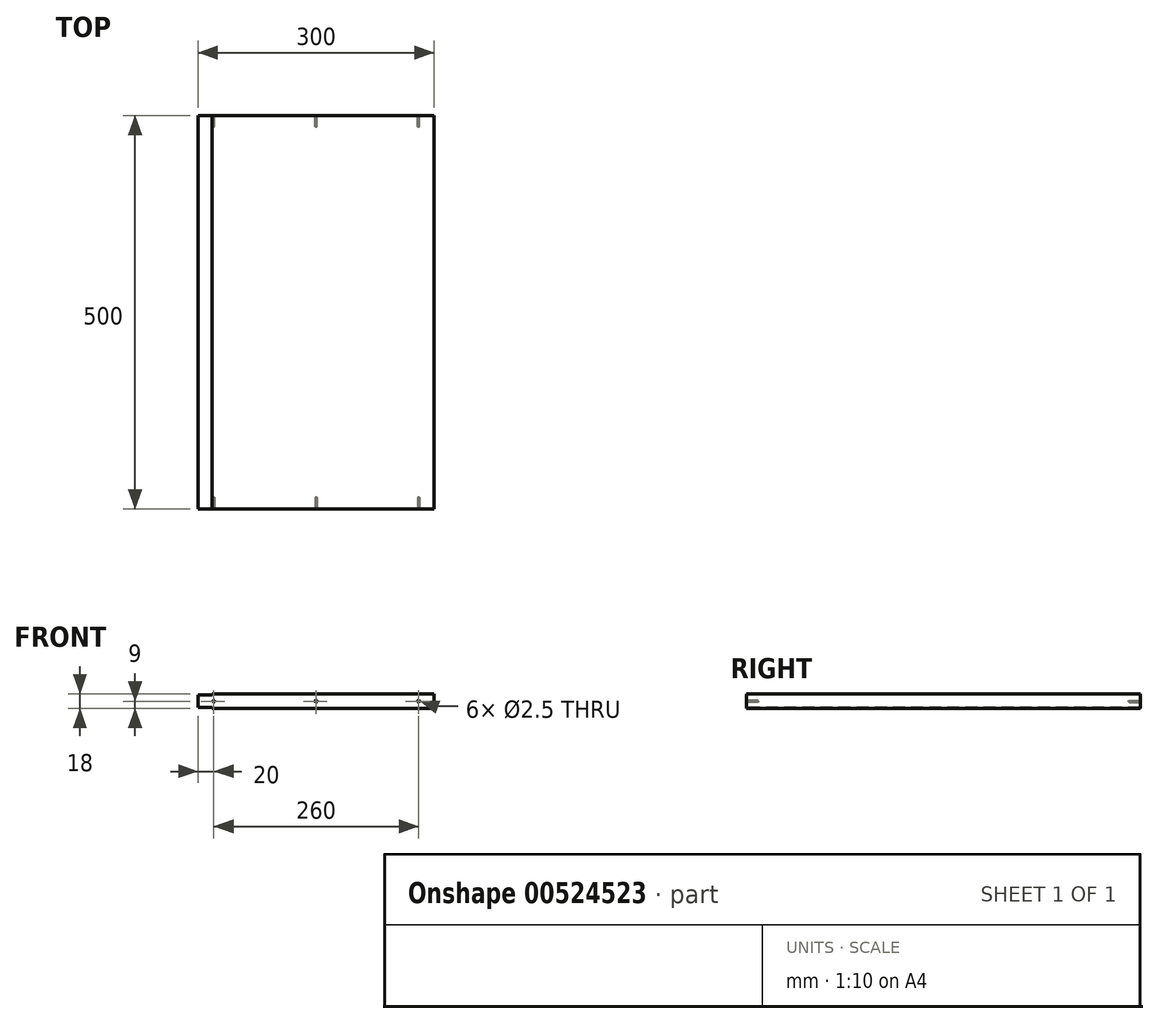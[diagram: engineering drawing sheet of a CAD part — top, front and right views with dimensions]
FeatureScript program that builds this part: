
annotation { "Feature Type Name" : "Feature", "Feature Type Description" : "" }
export const myFeature = defineFeature(function(context is Context, id is Id, definition is map)
    precondition{}
    {
        {
            var Q0;
            Q0=qCreatedBy(makeId("Top.planeOp"),FACE);
            var sketch = newSketch(context, id + "F0", { "sketchPlane" : qUnion([Q0])});
            skLineSegment(sketch, "E0.bottom", {"start": v(0, 0) * mm, "end": v(300, 0) * mm});
            skLineSegment(sketch, "E0.top", {"start": v(0, -500) * mm, "end": v(300, -500) * mm});
            skLineSegment(sketch, "E0.left", {"start": v(0, 0) * mm, "end": v(0, -500) * mm});
            skLineSegment(sketch, "E0.right", {"start": v(300, 0) * mm, "end": v(300, -500) * mm});
            skSolve(sketch);
        }
        {
            var Q0;
            Q0=qSketchRegion(id+"F0",true);
            extrude(context, id + "F1", {"entities" : qUnion([Q0]), "depth" : 18 * mm, "offsetDistance" : 25 * mm});
        }
        {
            var Q0;
            Q0=makeQuery(id+"F1.opExtrude","SWEPT_FACE",FACE,{"disambiguationData":[OSD([sQuery(id+"F0.wireOp",EDGE,"E0.top")])]});
            var sketch = newSketch(context, id + "F2", { "sketchPlane" : qUnion([Q0])});
            skPoint(sketch, "E1", {"position": v(20, 9) * mm});
            skPoint(sketch, "E2", {"position": v(150, 9) * mm});
            skPoint(sketch, "E3", {"position": v(280, 9) * mm});
            skSolve(sketch);
        }
        {
            var Q0;
            Q0=sQuery(id+"F2.wireOp",VERTEX,"E1");
            var Q1;
            Q1=sQuery(id+"F2.wireOp",VERTEX,"E2");
            var Q2;
            Q2=sQuery(id+"F2.wireOp",VERTEX,"E3");
            var Q3;
            Q3=makeQuery(id+"F1.opExtrude","SWEPT_BODY",BODY,{"disambiguationData":[OSD([sQuery(id+"F0.wireOp",EDGE,"E0.bottom"),sQuery(id+"F0.wireOp",EDGE,"E0.top"),sQuery(id+"F0.wireOp",EDGE,"E0.left"),sQuery(id+"F0.wireOp",EDGE,"E0.right")])]});
            hole(context, id + "F3", {"style" : HoleStyle.SIMPLE, "endStyle" : HoleEndStyle.BLIND, "standardTappedOrClearance" : lookupTablePath({ "standard" : "ISO", "engagement" : "75%", "pitch" : "0.5 mm", "size" : "M3", "type" : "Tapped" }), "standardBlindInLast" : lookupTablePath({ "standard" : "ISO", "engagement" : "75%", "pitch" : "0.5 mm", "size" : "M3", "type" : "Tapped" }), "holeDiameter" : 2.5 * mm, "showTappedDepth" : true, "holeDepth" : 14.5 * mm, "isTappedThrough" : true, "tappedDepth" : 13 * mm, "tapClearance" : 3, "locations" : qUnion([Q0, Q1, Q2]), "scope" : qUnion([Q3]), "majorDiameter" : 3 * mm});
        }
        {
            var Q0;
            Q0=makeQuery(id+"F1.opExtrude","SWEPT_FACE",FACE,{"disambiguationData":[OSD([sQuery(id+"F0.wireOp",EDGE,"E0.bottom")])]});
            var sketch = newSketch(context, id + "F4", { "sketchPlane" : qUnion([Q0])});
            skPoint(sketch, "E4", {"position": v(-280, 9) * mm});
            skPoint(sketch, "E5", {"position": v(-150, 9) * mm});
            skPoint(sketch, "E6", {"position": v(-20, 9) * mm});
            skSolve(sketch);
        }
        {
            var Q0;
            Q0=sQuery(id+"F4.wireOp",VERTEX,"E4");
            var Q1;
            Q1=sQuery(id+"F4.wireOp",VERTEX,"E5");
            var Q2;
            Q2=sQuery(id+"F4.wireOp",VERTEX,"E6");
            var Q3;
            Q3=makeQuery(id+"F1.opExtrude","SWEPT_BODY",BODY,{"disambiguationData":[OSD([sQuery(id+"F0.wireOp",EDGE,"E0.bottom"),sQuery(id+"F0.wireOp",EDGE,"E0.top"),sQuery(id+"F0.wireOp",EDGE,"E0.left"),sQuery(id+"F0.wireOp",EDGE,"E0.right")])]});
            hole(context, id + "F5", {"style" : HoleStyle.SIMPLE, "endStyle" : HoleEndStyle.BLIND, "standardTappedOrClearance" : lookupTablePath({ "standard" : "ISO", "engagement" : "75%", "pitch" : "0.5 mm", "size" : "M3", "type" : "Tapped" }), "standardBlindInLast" : lookupTablePath({ "standard" : "ISO", "engagement" : "75%", "pitch" : "0.5 mm", "size" : "M3", "type" : "Tapped" }), "holeDiameter" : 2.5 * mm, "showTappedDepth" : true, "holeDepth" : 14 * mm, "isTappedThrough" : true, "tappedDepth" : 12.5 * mm, "tapClearance" : 3, "locations" : qUnion([Q0, Q1, Q2]), "scope" : qUnion([Q3]), "majorDiameter" : 3 * mm});
        }
        {
            var Q0;
            Q0=makeQuery(id+"F1.opExtrude","SWEPT_FACE",FACE,{"disambiguationData":[OSD([sQuery(id+"F0.wireOp",EDGE,"E0.top")])]});
            var sketch = newSketch(context, id + "F6", { "sketchPlane" : qUnion([Q0])});
            skLineSegment(sketch, "E7.bottom", {"start": v(0, 18) * mm, "end": v(18, 18) * mm});
            skLineSegment(sketch, "E7.top", {"start": v(0, 17) * mm, "end": v(18, 17) * mm});
            skLineSegment(sketch, "E7.left", {"start": v(0, 18) * mm, "end": v(0, 17) * mm});
            skLineSegment(sketch, "E7.right", {"start": v(18, 18) * mm, "end": v(18, 17) * mm});
            skLineSegment(sketch, "E8.bottom", {"start": v(0, 0) * mm, "end": v(18, 0) * mm});
            skLineSegment(sketch, "E8.top", {"start": v(0, 1) * mm, "end": v(18, 1) * mm});
            skLineSegment(sketch, "E8.left", {"start": v(0, 0) * mm, "end": v(0, 1) * mm});
            skLineSegment(sketch, "E8.right", {"start": v(18, 0) * mm, "end": v(18, 1) * mm});
            skSolve(sketch);
        }
        {
            var Q0;
            Q0 = qSketchRegion(id + "F6", true);
            extrude(context, id + "F7", {"entities" : qUnion([Q0]), "operationType" : NewBodyOperationType.REMOVE, "endBound" : BoundingType.THROUGH_ALL, "oppositeDirection" : true, "depth" : 25 * mm, "offsetDistance" : 25 * mm});
        }
    });
